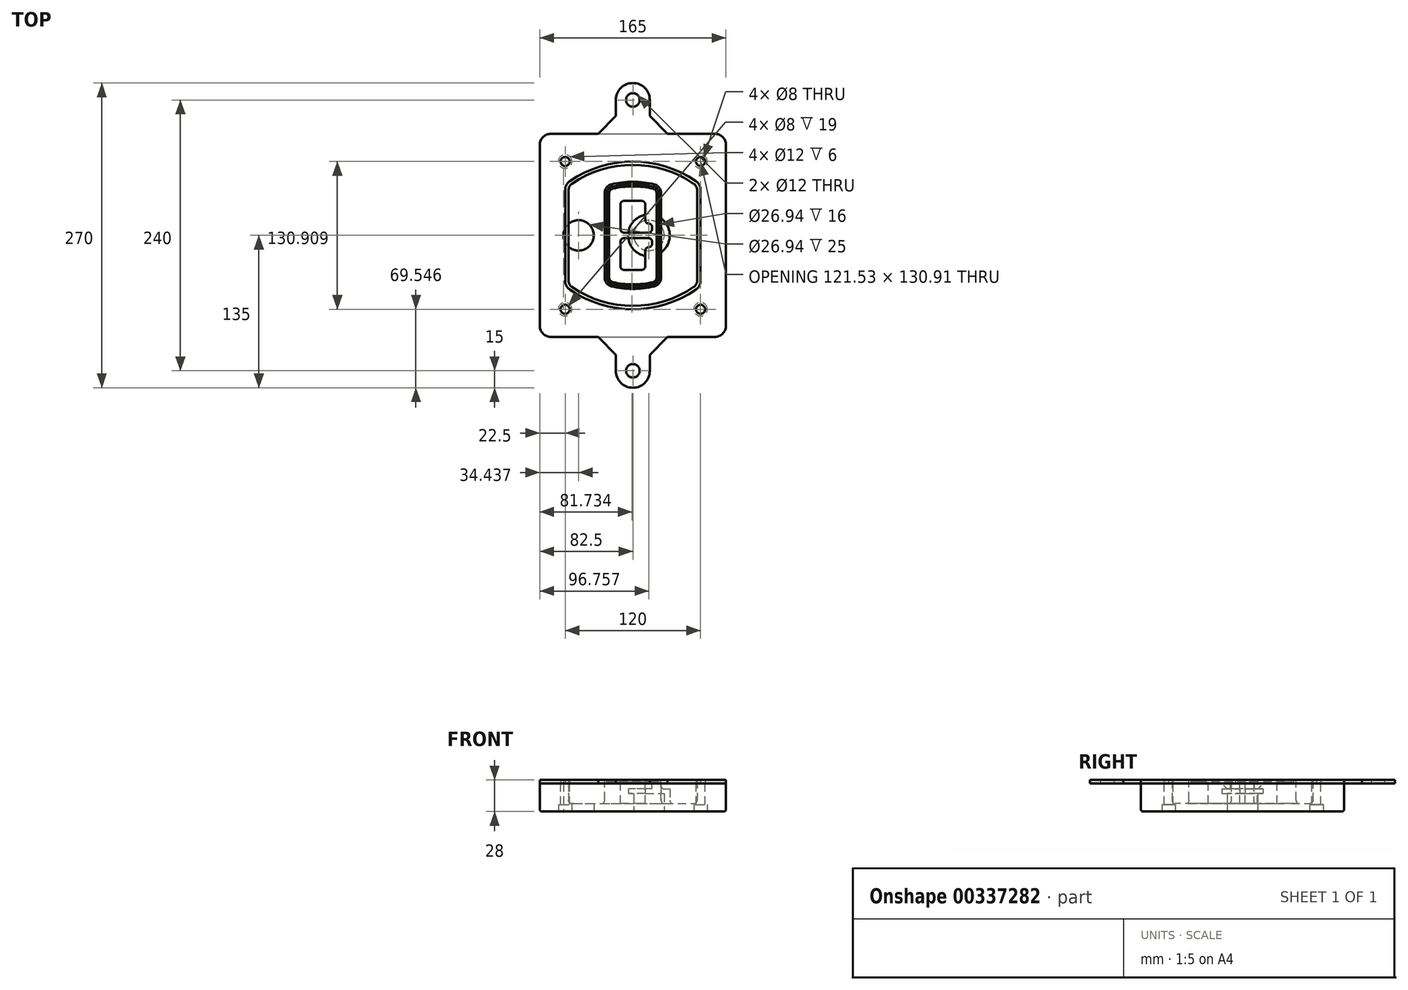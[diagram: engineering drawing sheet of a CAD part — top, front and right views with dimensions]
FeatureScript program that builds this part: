
annotation { "Feature Type Name" : "Feature", "Feature Type Description" : "" }
export const myFeature = defineFeature(function(context is Context, id is Id, definition is map)
    precondition{}
    {
        {
            var Q0;
            Q0=qCreatedBy(makeId("Top.planeOp"),FACE);
            var sketch = newSketch(context, id + "F0", { "sketchPlane" : qUnion([Q0])});
            skPoint(sketch, "E0.rect.middle", {"position": v(0, 0) * mm});
            skLineSegment(sketch, "E1.bottom", {"start": v(-72.5, -90) * mm, "end": v(72.5, -90) * mm});
            skLineSegment(sketch, "E1.top", {"start": v(-72.5, 90) * mm, "end": v(72.5, 90) * mm});
            skLineSegment(sketch, "E1.left", {"start": v(-82.5, -80) * mm, "end": v(-82.5, 80) * mm});
            skLineSegment(sketch, "E1.right", {"start": v(82.5, -80) * mm, "end": v(82.5, 80) * mm});
            skLineSegment(sketch, "E2", {"start": v(-82.5, 90) * mm, "end": v(82.5, -90) * mm, "construction": true});
            skLineSegment(sketch, "E3", {"start": v(82.5, 90) * mm, "end": v(-82.5, -90) * mm, "construction": true});
            skCircle(sketch, "E4", {"center": v(-60, 65.45) * mm, "radius": 4 * mm});
            skCircle(sketch, "E5", {"center": v(60, 65.45) * mm, "radius": 4 * mm});
            skCircle(sketch, "E6", {"center": v(60, -65.45) * mm, "radius": 4 * mm});
            skCircle(sketch, "E7", {"center": v(-60, -65.45) * mm, "radius": 4 * mm});
            skLineSegment(sketch, "E8", {"start": v(-60, 65.45) * mm, "end": v(60, 65.45) * mm, "construction": true});
            skLineSegment(sketch, "E9", {"start": v(60, 65.45) * mm, "end": v(60, -65.45) * mm, "construction": true});
            skLineSegment(sketch, "E10", {"start": v(60, -65.45) * mm, "end": v(-60, -65.45) * mm, "construction": true});
            skLineSegment(sketch, "E11", {"start": v(-60, -65.45) * mm, "end": v(-60, 65.45) * mm, "construction": true});
            skLineSegment(sketch, "E12", {"start": v(-60, 39.92) * mm, "end": v(-60, -39.92) * mm});
            skLineSegment(sketch, "E13", {"start": v(60, 39.92) * mm, "end": v(60, -39.92) * mm});
            skArc(sketch, "E14", {"start": v(55.67, 48.16) * mm, "mid": v(0, 65.45) * mm, "end": v(-55.67, 48.16) * mm});
            skArc(sketch, "E15", {"start": v(-55.67, -48.16) * mm, "mid": v(0, -65.45) * mm, "end": v(55.67, -48.16) * mm});
            skLineSegment(sketch, "E16", {"start": v(-60, 0) * mm, "end": v(60, 0) * mm, "construction": true});
            skPoint(sketch, "E17.visualSharp", {"position": v(-60, -45) * mm});
            skArc(sketch, "E17.filletArc", {"start": v(-60, -39.92) * mm, "mid": v(-58.85, -44.57) * mm, "end": v(-55.67, -48.16) * mm});
            skPoint(sketch, "E18.visualSharp", {"position": v(-60, 45) * mm});
            skArc(sketch, "E18.filletArc", {"start": v(-55.67, 48.16) * mm, "mid": v(-58.85, 44.57) * mm, "end": v(-60, 39.92) * mm});
            skPoint(sketch, "E19.visualSharp", {"position": v(60, 45) * mm});
            skArc(sketch, "E19.filletArc", {"start": v(60, 39.92) * mm, "mid": v(58.85, 44.57) * mm, "end": v(55.67, 48.16) * mm});
            skPoint(sketch, "E20.visualSharp", {"position": v(60, -45) * mm});
            skArc(sketch, "E20.filletArc", {"start": v(55.67, -48.16) * mm, "mid": v(58.85, -44.57) * mm, "end": v(60, -39.92) * mm});
            skPoint(sketch, "E21.visualSharp", {"position": v(-82.5, 90) * mm});
            skArc(sketch, "E21.filletArc", {"start": v(-72.5, 90) * mm, "mid": v(-79.57, 87.07) * mm, "end": v(-82.5, 80) * mm});
            skPoint(sketch, "E22.visualSharp", {"position": v(82.5, 90) * mm});
            skArc(sketch, "E22.filletArc", {"start": v(82.5, 80) * mm, "mid": v(79.57, 87.07) * mm, "end": v(72.5, 90) * mm});
            skPoint(sketch, "E23.visualSharp", {"position": v(82.5, -90) * mm});
            skArc(sketch, "E23.filletArc", {"start": v(72.5, -90) * mm, "mid": v(79.57, -87.07) * mm, "end": v(82.5, -80) * mm});
            skPoint(sketch, "E24.visualSharp", {"position": v(-82.5, -90) * mm});
            skArc(sketch, "E24.filletArc", {"start": v(-82.5, -80) * mm, "mid": v(-79.57, -87.07) * mm, "end": v(-72.5, -90) * mm});
            skArc(sketch, "E25.0", {"start": v(57, 39.92) * mm, "mid": v(56.2, 43.18) * mm, "end": v(53.97, 45.69) * mm});
            skLineSegment(sketch, "E25.1", {"start": v(57, 39.92) * mm, "end": v(57, -39.92) * mm});
            skArc(sketch, "E25.2", {"start": v(53.97, -45.69) * mm, "mid": v(56.2, -43.18) * mm, "end": v(57, -39.92) * mm});
            skArc(sketch, "E25.3", {"start": v(-53.97, -45.69) * mm, "mid": v(0, -62.45) * mm, "end": v(53.97, -45.69) * mm});
            skArc(sketch, "E25.4", {"start": v(-57, -39.92) * mm, "mid": v(-56.2, -43.18) * mm, "end": v(-53.97, -45.69) * mm});
            skArc(sketch, "E25.5", {"start": v(53.97, 45.69) * mm, "mid": v(0, 62.45) * mm, "end": v(-53.97, 45.69) * mm});
            skLineSegment(sketch, "E25.6", {"start": v(-57, 39.92) * mm, "end": v(-57, -39.92) * mm});
            skArc(sketch, "E25.7", {"start": v(-53.97, 45.69) * mm, "mid": v(-56.2, 43.18) * mm, "end": v(-57, 39.92) * mm});
            skArc(sketch, "E26.0", {"start": v(-57.93, 51.45) * mm, "mid": v(-62.4, 46.44) * mm, "end": v(-64, 39.92) * mm});
            skArc(sketch, "E26.1", {"start": v(57.93, 51.45) * mm, "mid": v(0, 69.45) * mm, "end": v(-57.93, 51.45) * mm});
            skArc(sketch, "E26.2", {"start": v(64, 39.92) * mm, "mid": v(62.4, 46.44) * mm, "end": v(57.93, 51.45) * mm});
            skLineSegment(sketch, "E26.3", {"start": v(64, 39.92) * mm, "end": v(64, -39.92) * mm});
            skArc(sketch, "E26.4", {"start": v(57.93, -51.45) * mm, "mid": v(62.4, -46.44) * mm, "end": v(64, -39.92) * mm});
            skLineSegment(sketch, "E26.5", {"start": v(-64, 39.92) * mm, "end": v(-64, -39.92) * mm});
            skArc(sketch, "E26.6", {"start": v(-57.93, -51.45) * mm, "mid": v(0, -69.45) * mm, "end": v(57.93, -51.45) * mm});
            skArc(sketch, "E26.7", {"start": v(-64, -39.92) * mm, "mid": v(-62.4, -46.44) * mm, "end": v(-57.93, -51.45) * mm});
            skSolve(sketch);
        }
        {
            var Q0;
            Q0=makeQuery(id+"F0.imprint","IMPRINT",FACE,{"disambiguationData":[TD([[makeQuery(id+"F0.imprint","IMPRINT",EDGE,{"derivedFrom":sQuery(id+"F0.wireOp",EDGE,"E1.bottom")}),1.0]])]});
            var Q1;
            Q1=makeQuery(id+"F0.imprint","IMPRINT",FACE,{"disambiguationData":[TD([[makeQuery(id+"F0.imprint","IMPRINT",EDGE,{"derivedFrom":sQuery(id+"F0.wireOp",EDGE,"E12")}),1.0]])]});
            var Q2;
            Q2=makeQuery(id+"F0.imprint","IMPRINT",FACE,{"disambiguationData":[TD([[makeQuery(id+"F0.imprint","IMPRINT",EDGE,{"derivedFrom":sQuery(id+"F0.wireOp",EDGE,"E25.0")}),1.0]])]});
            var Q3;
            Q3=makeQuery(id+"F0.imprint","IMPRINT",FACE,{"disambiguationData":[TD([[makeQuery(id+"F0.imprint","IMPRINT",EDGE,{"derivedFrom":sQuery(id+"F0.wireOp",EDGE,"E12")}),-1.0]])]});
            extrude(context, id + "F1", {"entities" : qUnion([Q0, Q1, Q2, Q3]), "oppositeDirection" : true, "depth" : 25 * mm});
        }
        {
            var Q0;
            Q0=makeQuery(id+"F0.imprint","IMPRINT",FACE,{"disambiguationData":[TD([[makeQuery(id+"F0.imprint","IMPRINT",EDGE,{"derivedFrom":sQuery(id+"F0.wireOp",EDGE,"E12")}),1.0]])]});
            extrude(context, id + "F2", {"entities" : qUnion([Q0]), "operationType" : NewBodyOperationType.ADD, "depth" : 3 * mm});
        }
        {
            var Q0;
            Q0=makeQuery(id+"F0.imprint","IMPRINT",FACE,{"disambiguationData":[TD([[makeQuery(id+"F0.imprint","IMPRINT",EDGE,{"derivedFrom":sQuery(id+"F0.wireOp",EDGE,"E25.0")}),1.0]])]});
            extrude(context, id + "F3", {"entities" : qUnion([Q0]), "operationType" : NewBodyOperationType.REMOVE, "oppositeDirection" : true, "depth" : 18 * mm});
        }
        {
            var Q0;
            Q0=makeQuery(id+"F2.opExtrude","CAP_FACE",FACE,{"disambiguationData":[OSD([sQuery(id+"F0.wireOp",EDGE,"E12"),sQuery(id+"F0.wireOp",EDGE,"E13"),sQuery(id+"F0.wireOp",EDGE,"E14"),sQuery(id+"F0.wireOp",EDGE,"E15"),sQuery(id+"F0.wireOp",EDGE,"E17.filletArc"),sQuery(id+"F0.wireOp",EDGE,"E18.filletArc"),sQuery(id+"F0.wireOp",EDGE,"E19.filletArc"),sQuery(id+"F0.wireOp",EDGE,"E20.filletArc"),sQuery(id+"F0.wireOp",EDGE,"E25.0"),sQuery(id+"F0.wireOp",EDGE,"E25.1"),sQuery(id+"F0.wireOp",EDGE,"E25.2"),sQuery(id+"F0.wireOp",EDGE,"E25.3"),sQuery(id+"F0.wireOp",EDGE,"E25.4"),sQuery(id+"F0.wireOp",EDGE,"E25.5"),sQuery(id+"F0.wireOp",EDGE,"E25.6"),sQuery(id+"F0.wireOp",EDGE,"E25.7")])],"isStart":false});
            var sketch = newSketch(context, id + "F4", { "sketchPlane" : qUnion([Q0])});
            skArc(sketch, "E27.0", {"start": v(-18.88, -45.2) * mm, "mid": v(0, -47.45) * mm, "end": v(18.88, -45.2) * mm});
            skArc(sketch, "E28.0", {"start": v(18.88, 45.2) * mm, "mid": v(0, 47.45) * mm, "end": v(-18.88, 45.2) * mm});
            skLineSegment(sketch, "E29", {"start": v(-25, 37.43) * mm, "end": v(-25, -37.43) * mm});
            skLineSegment(sketch, "E30", {"start": v(25, 37.43) * mm, "end": v(25, -37.43) * mm});
            skLineSegment(sketch, "E31", {"start": v(-25, 43.46) * mm, "end": v(25, 43.46) * mm, "construction": true});
            skLineSegment(sketch, "E32", {"start": v(-25, -43.46) * mm, "end": v(25, -43.46) * mm, "construction": true});
            skPoint(sketch, "E33.visualSharp", {"position": v(-25, 43.46) * mm});
            skArc(sketch, "E33.filletArc", {"start": v(-18.88, 45.2) * mm, "mid": v(-23.29, 42.37) * mm, "end": v(-25, 37.43) * mm});
            skPoint(sketch, "E34.visualSharp", {"position": v(25, 43.46) * mm});
            skArc(sketch, "E34.filletArc", {"start": v(25, 37.43) * mm, "mid": v(23.29, 42.37) * mm, "end": v(18.88, 45.2) * mm});
            skPoint(sketch, "E35.visualSharp", {"position": v(25, -43.46) * mm});
            skArc(sketch, "E35.filletArc", {"start": v(18.88, -45.2) * mm, "mid": v(23.29, -42.37) * mm, "end": v(25, -37.43) * mm});
            skPoint(sketch, "E36.visualSharp", {"position": v(-25, -43.46) * mm});
            skArc(sketch, "E36.filletArc", {"start": v(-25, -37.43) * mm, "mid": v(-23.29, -42.37) * mm, "end": v(-18.88, -45.2) * mm});
            skArc(sketch, "E37.0", {"start": v(53.97, 45.69) * mm, "mid": v(0, 62.45) * mm, "end": v(-53.97, 45.69) * mm});
            skArc(sketch, "E37.1", {"start": v(-53.97, 45.69) * mm, "mid": v(-56.2, 43.18) * mm, "end": v(-57, 39.92) * mm});
            skLineSegment(sketch, "E37.2", {"start": v(-57, 39.92) * mm, "end": v(-57, -39.92) * mm});
            skArc(sketch, "E37.3", {"start": v(-57, -39.92) * mm, "mid": v(-56.2, -43.18) * mm, "end": v(-53.97, -45.69) * mm});
            skArc(sketch, "E37.4", {"start": v(-53.97, -45.69) * mm, "mid": v(0, -62.45) * mm, "end": v(53.97, -45.69) * mm});
            skArc(sketch, "E37.5", {"start": v(53.97, -45.69) * mm, "mid": v(56.2, -43.18) * mm, "end": v(57, -39.92) * mm});
            skLineSegment(sketch, "E37.6", {"start": v(57, 39.92) * mm, "end": v(57, -39.92) * mm});
            skArc(sketch, "E37.7", {"start": v(57, 39.92) * mm, "mid": v(56.2, 43.18) * mm, "end": v(53.97, 45.69) * mm});
            skLineSegment(sketch, "E38.0", {"start": v(23, 37.43) * mm, "end": v(23, -37.43) * mm});
            skArc(sketch, "E38.1", {"start": v(18.41, -43.26) * mm, "mid": v(21.72, -41.14) * mm, "end": v(23, -37.43) * mm});
            skArc(sketch, "E38.2", {"start": v(-18.41, -43.26) * mm, "mid": v(0, -45.45) * mm, "end": v(18.41, -43.26) * mm});
            skArc(sketch, "E38.3", {"start": v(-23, -37.43) * mm, "mid": v(-21.72, -41.14) * mm, "end": v(-18.41, -43.26) * mm});
            skLineSegment(sketch, "E38.4", {"start": v(-23, 37.43) * mm, "end": v(-23, -37.43) * mm});
            skArc(sketch, "E38.5", {"start": v(23, 37.43) * mm, "mid": v(21.72, 41.14) * mm, "end": v(18.41, 43.26) * mm});
            skArc(sketch, "E38.6", {"start": v(-18.41, 43.26) * mm, "mid": v(-21.72, 41.14) * mm, "end": v(-23, 37.43) * mm});
            skArc(sketch, "E38.7", {"start": v(18.41, 43.26) * mm, "mid": v(0, 45.45) * mm, "end": v(-18.41, 43.26) * mm});
            skArc(sketch, "E39.0", {"start": v(21, 37.43) * mm, "mid": v(20.14, 39.9) * mm, "end": v(17.94, 41.31) * mm});
            skLineSegment(sketch, "E39.1", {"start": v(21, 37.43) * mm, "end": v(21, -37.43) * mm});
            skArc(sketch, "E39.2", {"start": v(17.94, -41.31) * mm, "mid": v(20.14, -39.9) * mm, "end": v(21, -37.43) * mm});
            skArc(sketch, "E39.3", {"start": v(-17.94, -41.31) * mm, "mid": v(0, -43.45) * mm, "end": v(17.94, -41.31) * mm});
            skArc(sketch, "E39.4", {"start": v(-21, -37.43) * mm, "mid": v(-20.14, -39.9) * mm, "end": v(-17.94, -41.31) * mm});
            skArc(sketch, "E39.5", {"start": v(17.94, 41.31) * mm, "mid": v(0, 43.45) * mm, "end": v(-17.94, 41.31) * mm});
            skLineSegment(sketch, "E39.6", {"start": v(-21, 37.43) * mm, "end": v(-21, -37.43) * mm});
            skArc(sketch, "E39.7", {"start": v(-17.94, 41.31) * mm, "mid": v(-20.14, 39.9) * mm, "end": v(-21, 37.43) * mm});
            skLineSegment(sketch, "E40", {"start": v(-25, 0) * mm, "end": v(25, 0) * mm, "construction": true});
            skLineSegment(sketch, "E41", {"start": v(-11, 5.5) * mm, "end": v(-11, 27.5) * mm});
            skLineSegment(sketch, "E42", {"start": v(-8, 30.5) * mm, "end": v(8, 30.5) * mm});
            skLineSegment(sketch, "E43", {"start": v(11, 27.5) * mm, "end": v(11, 13.5) * mm});
            skLineSegment(sketch, "E44", {"start": v(14, 10.5) * mm, "end": v(14, 10.5) * mm});
            skLineSegment(sketch, "E45", {"start": v(17, 7.5) * mm, "end": v(17, 5.5) * mm});
            skLineSegment(sketch, "E46", {"start": v(14, 2.5) * mm, "end": v(-8, 2.5) * mm});
            skPoint(sketch, "E47.visualSharp", {"position": v(-11, 30.5) * mm});
            skArc(sketch, "E47.filletArc", {"start": v(-8, 30.5) * mm, "mid": v(-10.12, 29.62) * mm, "end": v(-11, 27.5) * mm});
            skPoint(sketch, "E48.visualSharp", {"position": v(11, 30.5) * mm});
            skArc(sketch, "E48.filletArc", {"start": v(11, 27.5) * mm, "mid": v(10.12, 29.62) * mm, "end": v(8, 30.5) * mm});
            skPoint(sketch, "E49.visualSharp", {"position": v(11, 10.5) * mm});
            skArc(sketch, "E49.filletArc", {"start": v(11, 13.5) * mm, "mid": v(11.88, 11.38) * mm, "end": v(14, 10.5) * mm});
            skPoint(sketch, "E50.visualSharp", {"position": v(17, 10.5) * mm});
            skArc(sketch, "E50.filletArc", {"start": v(17, 7.5) * mm, "mid": v(16.12, 9.62) * mm, "end": v(14, 10.5) * mm});
            skPoint(sketch, "E51.visualSharp", {"position": v(17, 2.5) * mm});
            skArc(sketch, "E51.filletArc", {"start": v(14, 2.5) * mm, "mid": v(16.12, 3.38) * mm, "end": v(17, 5.5) * mm});
            skPoint(sketch, "E52.visualSharp", {"position": v(-11, 2.5) * mm});
            skArc(sketch, "E52.filletArc", {"start": v(-11, 5.5) * mm, "mid": v(-10.12, 3.38) * mm, "end": v(-8, 2.5) * mm});
            skLineSegment(sketch, "E53.0.MirrorCS", {"start": v(14, -2.5) * mm, "end": v(-8, -2.5) * mm});
            skArc(sketch, "E54.0.MirrorCS", {"start": v(-11, -5.5) * mm, "mid": v(-10.12, -3.38) * mm, "end": v(-8, -2.5) * mm});
            skLineSegment(sketch, "E55.0.MirrorCS", {"start": v(-11, -5.5) * mm, "end": v(-11, -27.5) * mm});
            skArc(sketch, "E56.0.MirrorCS", {"start": v(-8, -30.5) * mm, "mid": v(-10.12, -29.62) * mm, "end": v(-11, -27.5) * mm});
            skLineSegment(sketch, "E57.0.MirrorCS", {"start": v(-8, -30.5) * mm, "end": v(8, -30.5) * mm});
            skArc(sketch, "E58.0.MirrorCS", {"start": v(11, -27.5) * mm, "mid": v(10.12, -29.62) * mm, "end": v(8, -30.5) * mm});
            skLineSegment(sketch, "E59.0.MirrorCS", {"start": v(11, -27.5) * mm, "end": v(11, -13.5) * mm});
            skArc(sketch, "E60.0.MirrorCS", {"start": v(11, -13.5) * mm, "mid": v(11.88, -11.38) * mm, "end": v(14, -10.5) * mm});
            skArc(sketch, "E61.0.MirrorCS", {"start": v(17, -7.5) * mm, "mid": v(16.12, -9.62) * mm, "end": v(14, -10.5) * mm});
            skLineSegment(sketch, "E62.0.MirrorCS", {"start": v(17, -7.5) * mm, "end": v(17, -5.5) * mm});
            skArc(sketch, "E63.0.MirrorCS", {"start": v(14, -2.5) * mm, "mid": v(16.12, -3.38) * mm, "end": v(17, -5.5) * mm});
            skSolve(sketch);
        }
        {
            var Q0;
            Q0=makeQuery(id+"F4.imprint","IMPRINT",FACE,{"disambiguationData":[TD([[makeQuery(id+"F4.imprint","IMPRINT",EDGE,{"derivedFrom":sQuery(id+"F4.wireOp",EDGE,"E27.0")}),1.0]])]});
            var Q1;
            Q1=makeQuery(id+"F4.imprint","IMPRINT",FACE,{"disambiguationData":[TD([[makeQuery(id+"F4.imprint","IMPRINT",EDGE,{"derivedFrom":sQuery(id+"F4.wireOp",EDGE,"E38.0")}),-1.0]])]});
            var Q2;
            Q2=makeQuery(id+"F4.imprint","IMPRINT",FACE,{"disambiguationData":[TD([[makeQuery(id+"F4.imprint","IMPRINT",EDGE,{"derivedFrom":sQuery(id+"F4.wireOp",EDGE,"E39.0")}),1.0]])]});
            extrude(context, id + "F5", {"entities" : qUnion([Q0, Q1, Q2]), "operationType" : NewBodyOperationType.ADD, "endBound" : BoundingType.UP_TO_NEXT, "oppositeDirection" : true, "depth" : 25 * mm});
        }
        {
            var Q0;
            Q0=makeQuery(id+"F4.imprint","IMPRINT",FACE,{"disambiguationData":[TD([[makeQuery(id+"F4.imprint","IMPRINT",EDGE,{"derivedFrom":sQuery(id+"F4.wireOp",EDGE,"E38.0")}),-1.0]])]});
            extrude(context, id + "F6", {"entities" : qUnion([Q0]), "operationType" : NewBodyOperationType.REMOVE, "oppositeDirection" : true, "depth" : 2 * mm});
        }
        {
            var Q0;
            Q0=makeQuery(id+"F1.opExtrude","CAP_FACE",FACE,{"disambiguationData":[OSD([sQuery(id+"F0.wireOp",EDGE,"E1.bottom"),sQuery(id+"F0.wireOp",EDGE,"E1.top"),sQuery(id+"F0.wireOp",EDGE,"E1.left"),sQuery(id+"F0.wireOp",EDGE,"E1.right"),sQuery(id+"F0.wireOp",EDGE,"E4"),sQuery(id+"F0.wireOp",EDGE,"E5"),sQuery(id+"F0.wireOp",EDGE,"E6"),sQuery(id+"F0.wireOp",EDGE,"E7"),sQuery(id+"F0.wireOp",EDGE,"E21.filletArc"),sQuery(id+"F0.wireOp",EDGE,"E22.filletArc"),sQuery(id+"F0.wireOp",EDGE,"E23.filletArc"),sQuery(id+"F0.wireOp",EDGE,"E24.filletArc")])],"isStart":false});
            var sketch = newSketch(context, id + "F7", { "sketchPlane" : qUnion([Q0])});
            skCircle(sketch, "E64", {"center": v(14.26, 0) * mm, "radius": 13.47 * mm});
            skCircle(sketch, "E65", {"center": v(-48.06, 0) * mm, "radius": 13.47 * mm});
            skLineSegment(sketch, "E66", {"start": v(82.5, 0) * mm, "end": v(-82.5, 0) * mm});
            skCircle(sketch, "E67", {"center": v(14.26, 0) * mm, "radius": 18.47 * mm});
            skCircle(sketch, "E68", {"center": v(60, -65.45) * mm, "radius": 6 * mm});
            skCircle(sketch, "E69", {"center": v(-60, -65.45) * mm, "radius": 6 * mm});
            skCircle(sketch, "E70", {"center": v(-60, 65.45) * mm, "radius": 6 * mm});
            skCircle(sketch, "E71", {"center": v(60, 65.45) * mm, "radius": 6 * mm});
            skSolve(sketch);
        }
        {
            var Q0;
            {var subQ1=sQuery(id+"F7.wireOp",EDGE,"E66");var subQ4=sQuery(id+"F7.wireOp",EDGE,"E64");var subQ6=makeQuery(id+"F7.imprint","INTERSECT",VERTEX,{"disambiguationData":[OD(0.0)],"derivedFrom":[subQ4,subQ1]});Q0=makeQuery(id+"F7.imprint","IMPRINT",FACE,{"disambiguationData":[TD([[makeQuery(id+"F7.imprint","IMPRINT",EDGE,{"disambiguationData":[TD([[subQ6,-1.0]])],"derivedFrom":subQ4}),-1.0]])]});}
            var Q1;
            {var subQ0=sQuery(id+"F7.wireOp",EDGE,"E66");var subQ1=sQuery(id+"F7.wireOp",EDGE,"E64");var subQ3=makeQuery(id+"F7.imprint","INTERSECT",VERTEX,{"disambiguationData":[OD(0.0)],"derivedFrom":[subQ1,subQ0]});Q1=makeQuery(id+"F7.imprint","IMPRINT",FACE,{"disambiguationData":[TD([[makeQuery(id+"F7.imprint","IMPRINT",EDGE,{"disambiguationData":[TD([[subQ3,-1.0]])],"derivedFrom":subQ1}),1.0]])]});}
            var Q2;
            {var subQ0=sQuery(id+"F7.wireOp",EDGE,"E66");var subQ1=sQuery(id+"F7.wireOp",EDGE,"E64");var subQ3=makeQuery(id+"F7.imprint","INTERSECT",VERTEX,{"disambiguationData":[OD(0.0)],"derivedFrom":[subQ1,subQ0]});Q2=makeQuery(id+"F7.imprint","IMPRINT",FACE,{"disambiguationData":[TD([[makeQuery(id+"F7.imprint","IMPRINT",EDGE,{"disambiguationData":[TD([[subQ3,1.0]])],"derivedFrom":subQ1}),1.0]])]});}
            var Q3;
            {var subQ1=sQuery(id+"F7.wireOp",EDGE,"E66");var subQ4=sQuery(id+"F7.wireOp",EDGE,"E64");var subQ6=makeQuery(id+"F7.imprint","INTERSECT",VERTEX,{"disambiguationData":[OD(0.0)],"derivedFrom":[subQ4,subQ1]});Q3=makeQuery(id+"F7.imprint","IMPRINT",FACE,{"disambiguationData":[TD([[makeQuery(id+"F7.imprint","IMPRINT",EDGE,{"disambiguationData":[TD([[subQ6,1.0]])],"derivedFrom":subQ4}),-1.0]])]});}
            extrude(context, id + "F8", {"entities" : qUnion([Q0, Q1, Q2, Q3]), "operationType" : NewBodyOperationType.ADD, "oppositeDirection" : true, "depth" : 20 * mm});
        }
        {
            var Q0;
            {var subQ0=sQuery(id+"F7.wireOp",EDGE,"E66");var subQ1=sQuery(id+"F7.wireOp",EDGE,"E64");var subQ3=makeQuery(id+"F7.imprint","INTERSECT",VERTEX,{"disambiguationData":[OD(0.0)],"derivedFrom":[subQ1,subQ0]});Q0=makeQuery(id+"F7.imprint","IMPRINT",FACE,{"disambiguationData":[TD([[makeQuery(id+"F7.imprint","IMPRINT",EDGE,{"disambiguationData":[TD([[subQ3,-1.0]])],"derivedFrom":subQ1}),1.0]])]});}
            var Q1;
            {var subQ0=sQuery(id+"F7.wireOp",EDGE,"E66");var subQ1=sQuery(id+"F7.wireOp",EDGE,"E64");var subQ3=makeQuery(id+"F7.imprint","INTERSECT",VERTEX,{"disambiguationData":[OD(0.0)],"derivedFrom":[subQ1,subQ0]});Q1=makeQuery(id+"F7.imprint","IMPRINT",FACE,{"disambiguationData":[TD([[makeQuery(id+"F7.imprint","IMPRINT",EDGE,{"disambiguationData":[TD([[subQ3,1.0]])],"derivedFrom":subQ1}),1.0]])]});}
            extrude(context, id + "F9", {"entities" : qUnion([Q0, Q1]), "operationType" : NewBodyOperationType.REMOVE, "oppositeDirection" : true, "depth" : 16 * mm});
        }
        {
            var Q0;
            {var subQ0=sQuery(id+"F7.wireOp",EDGE,"E66");var subQ1=sQuery(id+"F7.wireOp",EDGE,"E65");var subQ3=makeQuery(id+"F7.imprint","INTERSECT",VERTEX,{"disambiguationData":[OD(0.0)],"derivedFrom":[subQ1,subQ0]});Q0=makeQuery(id+"F7.imprint","IMPRINT",FACE,{"disambiguationData":[TD([[makeQuery(id+"F7.imprint","IMPRINT",EDGE,{"disambiguationData":[TD([[subQ3,-1.0]])],"derivedFrom":subQ1}),1.0]])]});}
            var Q1;
            {var subQ0=sQuery(id+"F7.wireOp",EDGE,"E66");var subQ1=sQuery(id+"F7.wireOp",EDGE,"E65");var subQ3=makeQuery(id+"F7.imprint","INTERSECT",VERTEX,{"disambiguationData":[OD(0.0)],"derivedFrom":[subQ1,subQ0]});Q1=makeQuery(id+"F7.imprint","IMPRINT",FACE,{"disambiguationData":[TD([[makeQuery(id+"F7.imprint","IMPRINT",EDGE,{"disambiguationData":[TD([[subQ3,1.0]])],"derivedFrom":subQ1}),1.0]])]});}
            extrude(context, id + "F10", {"entities" : qUnion([Q0, Q1]), "operationType" : NewBodyOperationType.REMOVE, "oppositeDirection" : true, "depth" : 25 * mm});
        }
        {
            var Q0;
            Q0=makeQuery(id+"F7.imprint","IMPRINT",FACE,{"disambiguationData":[TD([[makeQuery(id+"F7.imprint","IMPRINT",EDGE,{"derivedFrom":sQuery(id+"F7.wireOp",EDGE,"E68")}),1.0]])]});
            var Q1;
            Q1=makeQuery(id+"F7.imprint","IMPRINT",FACE,{"disambiguationData":[TD([[makeQuery(id+"F7.imprint","IMPRINT",EDGE,{"derivedFrom":makeQuery(id+"F1.opExtrude","CAP_EDGE",EDGE,{"disambiguationData":[OSD([sQuery(id+"F0.wireOp",EDGE,"E5")])],"isStart":false})}),-1.0]])]});
            var Q2;
            Q2=makeQuery(id+"F7.imprint","IMPRINT",FACE,{"disambiguationData":[TD([[makeQuery(id+"F7.imprint","IMPRINT",EDGE,{"derivedFrom":sQuery(id+"F7.wireOp",EDGE,"E69")}),1.0]])]});
            var Q3;
            Q3=makeQuery(id+"F7.imprint","IMPRINT",FACE,{"disambiguationData":[TD([[makeQuery(id+"F7.imprint","IMPRINT",EDGE,{"derivedFrom":makeQuery(id+"F1.opExtrude","CAP_EDGE",EDGE,{"disambiguationData":[OSD([sQuery(id+"F0.wireOp",EDGE,"E4")])],"isStart":false})}),-1.0]])]});
            var Q4;
            Q4=makeQuery(id+"F7.imprint","IMPRINT",FACE,{"disambiguationData":[TD([[makeQuery(id+"F7.imprint","IMPRINT",EDGE,{"derivedFrom":sQuery(id+"F7.wireOp",EDGE,"E70")}),1.0]])]});
            var Q5;
            Q5=makeQuery(id+"F7.imprint","IMPRINT",FACE,{"disambiguationData":[TD([[makeQuery(id+"F7.imprint","IMPRINT",EDGE,{"derivedFrom":makeQuery(id+"F1.opExtrude","CAP_EDGE",EDGE,{"disambiguationData":[OSD([sQuery(id+"F0.wireOp",EDGE,"E7")])],"isStart":false})}),-1.0]])]});
            var Q6;
            Q6=makeQuery(id+"F7.imprint","IMPRINT",FACE,{"disambiguationData":[TD([[makeQuery(id+"F7.imprint","IMPRINT",EDGE,{"derivedFrom":sQuery(id+"F7.wireOp",EDGE,"E71")}),1.0]])]});
            var Q7;
            Q7=makeQuery(id+"F7.imprint","IMPRINT",FACE,{"disambiguationData":[TD([[makeQuery(id+"F7.imprint","IMPRINT",EDGE,{"derivedFrom":makeQuery(id+"F1.opExtrude","CAP_EDGE",EDGE,{"disambiguationData":[OSD([sQuery(id+"F0.wireOp",EDGE,"E6")])],"isStart":false})}),-1.0]])]});
            extrude(context, id + "F11", {"entities" : qUnion([Q0, Q1, Q2, Q3, Q4, Q5, Q6, Q7]), "operationType" : NewBodyOperationType.REMOVE, "oppositeDirection" : true, "depth" : 6 * mm});
        }
        {
            var Q0;
            Q0=makeQuery(id+"F9.boolean.opBoolean","COPY",FACE,{"derivedFrom":makeQuery(id+"F9.opExtrude","CAP_FACE",FACE,{"disambiguationData":[OSD([sQuery(id+"F7.wireOp",EDGE,"E64")])],"isStart":false})});
            var sketch = newSketch(context, id + "F12", { "sketchPlane" : qUnion([Q0])});
            skArc(sketch, "E72.0", {"start": v(11, 18.18) * mm, "mid": v(0.93, 12.79) * mm, "end": v(-4.04, 2.5) * mm});
            skArc(sketch, "E72.1", {"start": v(-4.04, -2.5) * mm, "mid": v(0.93, -12.79) * mm, "end": v(11, -18.18) * mm});
            skLineSegment(sketch, "E73", {"start": v(-4.04, -2.5) * mm, "end": v(14, -2.5) * mm});
            skLineSegment(sketch, "E74.0", {"start": v(14, 2.5) * mm, "end": v(-4.04, 2.5) * mm});
            skArc(sketch, "E74.1", {"start": v(14, 2.5) * mm, "mid": v(16.12, 3.38) * mm, "end": v(17, 5.5) * mm});
            skLineSegment(sketch, "E74.2", {"start": v(17, 7.5) * mm, "end": v(17, 5.5) * mm});
            skArc(sketch, "E74.3", {"start": v(17, 7.5) * mm, "mid": v(16.12, 9.62) * mm, "end": v(14, 10.5) * mm});
            skArc(sketch, "E74.4", {"start": v(11, 13.5) * mm, "mid": v(11.88, 11.38) * mm, "end": v(14, 10.5) * mm});
            skLineSegment(sketch, "E74.5", {"start": v(11, 18.18) * mm, "end": v(11, 13.5) * mm});
            skLineSegment(sketch, "E74.7", {"start": v(14, -2.5) * mm, "end": v(-4.04, -2.5) * mm});
            skArc(sketch, "E74.8", {"start": v(14, -2.5) * mm, "mid": v(16.12, -3.38) * mm, "end": v(17, -5.5) * mm});
            skLineSegment(sketch, "E74.9", {"start": v(17, -7.5) * mm, "end": v(17, -5.5) * mm});
            skArc(sketch, "E74.10", {"start": v(17, -7.5) * mm, "mid": v(16.12, -9.62) * mm, "end": v(14, -10.5) * mm});
            skArc(sketch, "E74.11", {"start": v(11, -13.5) * mm, "mid": v(11.88, -11.38) * mm, "end": v(14, -10.5) * mm});
            skLineSegment(sketch, "E74.12", {"start": v(11, -18.18) * mm, "end": v(11, -13.5) * mm});
            skPoint(sketch, "E75.orphan", {"position": v(11, -27.5) * mm});
            skPoint(sketch, "E76.orphan", {"position": v(-8, -2.5) * mm});
            skPoint(sketch, "E77.orphan", {"position": v(-8, 2.5) * mm});
            skPoint(sketch, "E78.orphan", {"position": v(11, 27.5) * mm});
            skSolve(sketch);
        }
        {
            var Q0;
            {var subQ7=sQuery(id+"F12.wireOp",EDGE,"E72.0");var subQ14=sQuery(id+"F12.wireOp",EDGE,"E72.1");var subQ16=sQuery(id+"F12.wireOp",EDGE,"E74.1");var subQ18=sQuery(id+"F12.wireOp",EDGE,"E74.8");Q0=qUnion([makeQuery(id+"F12.imprint","IMPRINT",FACE,{"disambiguationData":[TD([[makeQuery(id+"F12.imprint","IMPRINT",EDGE,{"derivedFrom":subQ7}),1.0]])]}),makeQuery(id+"F12.imprint","IMPRINT",FACE,{"disambiguationData":[TD([[makeQuery(id+"F12.imprint","IMPRINT",EDGE,{"derivedFrom":subQ14}),1.0]])]}),makeQuery(id+"F12.imprint","IMPRINT",FACE,{"disambiguationData":[TD([[makeQuery(id+"F12.imprint","IMPRINT",EDGE,{"derivedFrom":subQ16}),1.0]])]}),makeQuery(id+"F12.imprint","IMPRINT",FACE,{"disambiguationData":[TD([[makeQuery(id+"F12.imprint","IMPRINT",EDGE,{"derivedFrom":subQ18}),-1.0]])]})]);}
            var Q1;
            Q1=makeQuery(id+"F5.boolean.opBoolean","SPLIT",FACE,{"disambiguationData":[TD([makeQuery(id+"F5.opExtrude","SWEPT_FACE",FACE,{"disambiguationData":[OSD([sQuery(id+"F4.wireOp",EDGE,"E41")])]})])],"derivedFrom":makeQuery(id+"F3.boolean.opBoolean","COPY",FACE,{"derivedFrom":makeQuery(id+"F3.opExtrude","CAP_FACE",FACE,{"disambiguationData":[OSD([sQuery(id+"F0.wireOp",EDGE,"E25.0"),sQuery(id+"F0.wireOp",EDGE,"E25.1"),sQuery(id+"F0.wireOp",EDGE,"E25.2"),sQuery(id+"F0.wireOp",EDGE,"E25.3"),sQuery(id+"F0.wireOp",EDGE,"E25.4"),sQuery(id+"F0.wireOp",EDGE,"E25.5"),sQuery(id+"F0.wireOp",EDGE,"E25.6"),sQuery(id+"F0.wireOp",EDGE,"E25.7")])],"isStart":false})})});
            extrude(context, id + "F13", {"entities" : qUnion([Q0]), "operationType" : NewBodyOperationType.REMOVE, "endBound" : BoundingType.UP_TO_SURFACE, "endBoundEntityFace" : qUnion([Q1]), "depth" : 25 * mm});
        }
        {
            var Q0;
            Q0=makeQuery(id+"F3.boolean.opBoolean","COPY",EDGE,{"derivedFrom":makeQuery(id+"F3.opExtrude","CAP_EDGE",EDGE,{"disambiguationData":[OSD([sQuery(id+"F0.wireOp",EDGE,"E25.6")])],"isStart":false})});
            var Q1;
            Q1=makeQuery(id+"F8.boolean.opBoolean","INTERSECT",EDGE,{"derivedFrom":[makeQuery(id+"F5.opExtrude","SWEPT_FACE",FACE,{"disambiguationData":[OSD([sQuery(id+"F4.wireOp",EDGE,"E30")])]}),makeQuery(id+"F8.opExtrude","CAP_FACE",FACE,{"disambiguationData":[OSD([sQuery(id+"F7.wireOp",EDGE,"E67")])],"isStart":false})]});
            var Q2;
            Q2=makeQuery(id+"F8.boolean.opBoolean","INTERSECT",EDGE,{"disambiguationData":[OD(1.0)],"derivedFrom":[makeQuery(id+"F5.opExtrude","SWEPT_FACE",FACE,{"disambiguationData":[OSD([sQuery(id+"F4.wireOp",EDGE,"E30")])]}),makeQuery(id+"F8.opExtrude","SWEPT_FACE",FACE,{"disambiguationData":[OSD([sQuery(id+"F7.wireOp",EDGE,"E67")])]})]});
            var Q3;
            {var subQ0=sQuery(id+"F4.wireOp",EDGE,"E30");Q3=makeQuery(id+"F8.boolean.opBoolean","SPLIT",EDGE,{"disambiguationData":[TD([makeQuery(id+"F5.opExtrude","SWEPT_FACE",FACE,{"disambiguationData":[OSD([sQuery(id+"F4.wireOp",EDGE,"E35.filletArc")])]})])],"derivedFrom":makeQuery(id+"F5.opExtrude","CAP_EDGE",EDGE,{"disambiguationData":[OSD([subQ0])],"isStart":false})});}
            var Q4;
            {var subQ0=sQuery(id+"F0.wireOp",EDGE,"E25.7");var subQ1=sQuery(id+"F0.wireOp",EDGE,"E25.1");var subQ2=sQuery(id+"F0.wireOp",EDGE,"E25.6");var subQ3=sQuery(id+"F0.wireOp",EDGE,"E25.5");var subQ4=sQuery(id+"F0.wireOp",EDGE,"E25.4");var subQ5=sQuery(id+"F0.wireOp",EDGE,"E25.0");var subQ6=sQuery(id+"F0.wireOp",EDGE,"E25.2");var subQ7=sQuery(id+"F0.wireOp",EDGE,"E25.3");Q4=makeQuery(id+"F8.boolean.opBoolean","INTERSECT",EDGE,{"derivedFrom":[makeQuery(id+"F5.boolean.opBoolean","SPLIT",FACE,{"disambiguationData":[TD([makeQuery(id+"F2.opExtrude","SWEPT_FACE",FACE,{"disambiguationData":[OSD([subQ5])]})])],"derivedFrom":makeQuery(id+"F3.boolean.opBoolean","COPY",FACE,{"derivedFrom":makeQuery(id+"F3.opExtrude","CAP_FACE",FACE,{"disambiguationData":[OSD([subQ5,subQ1,subQ6,subQ7,subQ4,subQ3,subQ2,subQ0])],"isStart":false})})}),makeQuery(id+"F8.opExtrude","SWEPT_FACE",FACE,{"disambiguationData":[OSD([sQuery(id+"F7.wireOp",EDGE,"E67")])]})]});}
            var Q5;
            Q5=makeQuery(id+"F8.boolean.opBoolean","INTERSECT",EDGE,{"disambiguationData":[OD(0.0)],"derivedFrom":[makeQuery(id+"F5.opExtrude","SWEPT_FACE",FACE,{"disambiguationData":[OSD([sQuery(id+"F4.wireOp",EDGE,"E30")])]}),makeQuery(id+"F8.opExtrude","SWEPT_FACE",FACE,{"disambiguationData":[OSD([sQuery(id+"F7.wireOp",EDGE,"E67")])]})]});
            fillet(context, id + "F14", {"entities" : qUnion([Q0, Q1, Q2, Q3, Q4, Q5]), "radius" : 3 * mm, "tangentPropagation" : true, "allowEdgeOverflow" : false});
        }
        {
            var Q0;
            Q0=makeQuery(id+"F1.opExtrude","CAP_EDGE",EDGE,{"disambiguationData":[OSD([sQuery(id+"F0.wireOp",EDGE,"E1.bottom")])],"isStart":false});
            fillet(context, id + "F15", {"entities" : qUnion([Q0]), "radius" : 2 * mm, "tangentPropagation" : true, "allowEdgeOverflow" : false});
        }
        {
            var Q0;
            {var subQ0=sQuery(id+"F0.wireOp",EDGE,"E21.filletArc");var subQ1=sQuery(id+"F0.wireOp",EDGE,"E7");var subQ2=sQuery(id+"F0.wireOp",EDGE,"E6");var subQ3=sQuery(id+"F0.wireOp",EDGE,"E5");var subQ4=sQuery(id+"F0.wireOp",EDGE,"E4");var subQ5=sQuery(id+"F0.wireOp",EDGE,"E22.filletArc");var subQ6=sQuery(id+"F0.wireOp",EDGE,"E1.bottom");var subQ7=sQuery(id+"F0.wireOp",EDGE,"E1.right");var subQ8=sQuery(id+"F0.wireOp",EDGE,"E1.top");var subQ9=sQuery(id+"F0.wireOp",EDGE,"E1.left");var subQ10=sQuery(id+"F0.wireOp",EDGE,"E23.filletArc");var subQ11=sQuery(id+"F0.wireOp",EDGE,"E24.filletArc");Q0=makeQuery(id+"F2.boolean.opBoolean","SPLIT",FACE,{"disambiguationData":[TD([makeQuery(id+"F1.opExtrude","SWEPT_FACE",FACE,{"disambiguationData":[OSD([subQ6])]})])],"derivedFrom":makeQuery(id+"F1.opExtrude","CAP_FACE",FACE,{"disambiguationData":[OSD([subQ6,subQ8,subQ9,subQ7,subQ4,subQ3,subQ2,subQ1,subQ0,subQ5,subQ10,subQ11])],"isStart":true})});}
            var sketch = newSketch(context, id + "F16", { "sketchPlane" : qUnion([Q0])});
            skLineSegment(sketch, "E79", {"start": v(-30.74, 90) * mm, "end": v(-15, 105.74) * mm});
            skLineSegment(sketch, "E80", {"start": v(30.74, 90) * mm, "end": v(15, 105.74) * mm});
            skLineSegment(sketch, "E81", {"start": v(-15, 105.74) * mm, "end": v(-15, 120) * mm});
            skLineSegment(sketch, "E82", {"start": v(15, 105.74) * mm, "end": v(15, 120) * mm});
            skArc(sketch, "E83", {"start": v(15, 120) * mm, "mid": v(0, 135) * mm, "end": v(-15, 120) * mm});
            skLineSegment(sketch, "E84", {"start": v(0, 120) * mm, "end": v(0, 90) * mm, "construction": true});
            skCircle(sketch, "E85", {"center": v(0, 120) * mm, "radius": 6 * mm});
            skLineSegment(sketch, "E86", {"start": v(-82.5, 0) * mm, "end": v(82.5, 0) * mm, "construction": true});
            skLineSegment(sketch, "E87.MirrorCS", {"start": v(-30.74, -90) * mm, "end": v(-15, -105.74) * mm});
            skLineSegment(sketch, "E88.MirrorCS", {"start": v(-15, -105.74) * mm, "end": v(-15, -120) * mm});
            skArc(sketch, "E89.MirrorCS", {"start": v(15, -120) * mm, "mid": v(0, -135) * mm, "end": v(-15, -120) * mm});
            skLineSegment(sketch, "E90.MirrorCS", {"start": v(15, -105.74) * mm, "end": v(15, -120) * mm});
            skLineSegment(sketch, "E91.MirrorCS", {"start": v(30.74, -90) * mm, "end": v(15, -105.74) * mm});
            skCircle(sketch, "E92.MirrorC", {"center": v(0, -120) * mm, "radius": 6 * mm});
            skLineSegment(sketch, "E93.MirrorCS", {"start": v(0, -120) * mm, "end": v(0, -90) * mm, "construction": true});
            skSolve(sketch);
        }
        {
            var Q0;
            {var subQ0=sQuery(id+"F16.wireOp",EDGE,"E79");Q0=makeQuery(id+"F16.imprint","IMPRINT",FACE,{"disambiguationData":[TD([[makeQuery(id+"F16.imprint","IMPRINT",EDGE,{"derivedFrom":subQ0}),-1.0]])]});}
            var Q1;
            Q1=makeQuery(id+"F16.imprint","IMPRINT",FACE,{"disambiguationData":[TD([[makeQuery(id+"F16.imprint","IMPRINT",EDGE,{"derivedFrom":makeQuery(id+"F1.opExtrude","CAP_EDGE",EDGE,{"disambiguationData":[OSD([sQuery(id+"F0.wireOp",EDGE,"E1.left")])],"isStart":true})}),-1.0]])]});
            var Q2;
            {var subQ0=sQuery(id+"F16.wireOp",EDGE,"E87.MirrorCS");Q2=makeQuery(id+"F16.imprint","IMPRINT",FACE,{"disambiguationData":[TD([[makeQuery(id+"F16.imprint","IMPRINT",EDGE,{"derivedFrom":subQ0}),1.0]])]});}
            var Q3;
            Q3=makeQuery(id+"F2.opExtrude","CAP_FACE",FACE,{"disambiguationData":[OSD([sQuery(id+"F0.wireOp",EDGE,"E12"),sQuery(id+"F0.wireOp",EDGE,"E13"),sQuery(id+"F0.wireOp",EDGE,"E14"),sQuery(id+"F0.wireOp",EDGE,"E15"),sQuery(id+"F0.wireOp",EDGE,"E17.filletArc"),sQuery(id+"F0.wireOp",EDGE,"E18.filletArc"),sQuery(id+"F0.wireOp",EDGE,"E19.filletArc"),sQuery(id+"F0.wireOp",EDGE,"E20.filletArc"),sQuery(id+"F0.wireOp",EDGE,"E25.0"),sQuery(id+"F0.wireOp",EDGE,"E25.1"),sQuery(id+"F0.wireOp",EDGE,"E25.2"),sQuery(id+"F0.wireOp",EDGE,"E25.3"),sQuery(id+"F0.wireOp",EDGE,"E25.4"),sQuery(id+"F0.wireOp",EDGE,"E25.5"),sQuery(id+"F0.wireOp",EDGE,"E25.6"),sQuery(id+"F0.wireOp",EDGE,"E25.7")])],"isStart":false});
            extrude(context, id + "F17", {"entities" : qUnion([Q0, Q1, Q2]), "endBound" : BoundingType.UP_TO_SURFACE, "endBoundEntityFace" : qUnion([Q3]), "depth" : 25 * mm});
        }
    });
